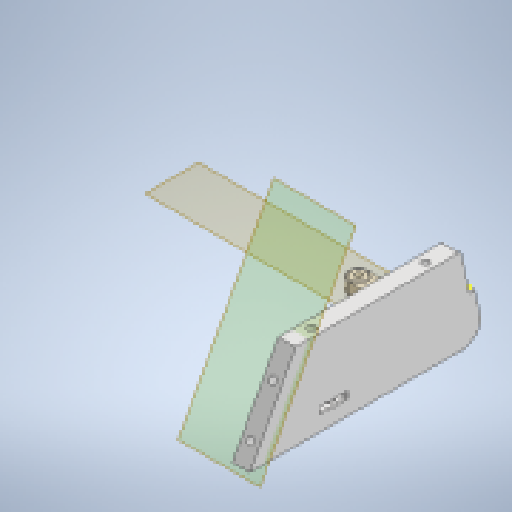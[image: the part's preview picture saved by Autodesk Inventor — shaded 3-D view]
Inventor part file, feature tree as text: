
AUTODESK INVENTOR PART (.ipt)
format: ipt  version: 2023 (Build 270158000, 158)  size: 718,848 bytes
history: native  units: in
note: dims shown in document units (in); Inventor stores cm internally (conversion verified against a paired STEP export)
features: sketch x35, other x12, extrude x6, projected_geometry x4, fillet x1, reference x1
ambient origin geometry x8: Origin, YZ Plane, XZ Plane, XY Plane, X Axis, Y Axis, Z Axis, Center Point
bodies: Body1 (feature_tree)
feature tree (59):
  other  "sciana_awaryjna.ipt"
  extrude  "Wyciągnięcie proste1"  Depth=0.3937in
  extrude  "Wyciągnięcie proste2"  Depth=0.3937in TaperAngle=0.0deg
  extrude  "Wyciągnięcie proste3"  Depth=0.0039in TaperAngle=0.0deg
  extrude  "Wyciągnięcie proste4"  Depth=0.0394in
  fillet  "Zaokrąglenie1"  Radius=0.0197in
  extrude  "Wyciągnięcie proste5"  TaperAngle=0.0deg  [1 undecoded]
  extrude  "Wyciągnięcie proste6"  Depth=0.0118in
  other  "Bryła1::sciana_awaryjna.ipt"
  other  "Bryła wyprowadzona1"
  sketch  "Szkic1"
  sketch  "Szkic2"
  sketch  "Szkic3"
  sketch  "Szkic4"
  sketch  "Szkic5"
  sketch  "Szkic6"
  sketch  "Szkic7"
  sketch  "Szkic8"
  sketch  "Szkic9"
  sketch  "Szkic12"
  sketch  "Szkic13"
  sketch  "Szkic14"
  sketch  "Szkic15"
  sketch  "Szkic16"
  sketch  "Szkic17"
  sketch  "Szkic18"
  sketch  "Szkic19"
  sketch  "Szkic20"
  sketch  "Szkic21"
  sketch  "Szkic22"
  sketch  "Szkic23"
  sketch  "Szkic24"
  sketch  "Szkic25"
  sketch  "Szkic26"
  sketch  "Szkic27"
  sketch  "Szkic28"
  sketch  "Szkic29"
  sketch  "Szkic30"
  sketch  "Szkic31"
  other  "Płaszczyzna konstrukcyjna1"
  other  "Płaszczyzna konstrukcyjna2"
  other  "Płaszczyzna konstrukcyjna3"
  other  "Płaszczyzna konstrukcyjna4"
  sketch  "Szkic32"
  projected_geometry  "Pętla rzutowana1"
  sketch  "Szkic33"
  projected_geometry  "Pętla rzutowana2"
  sketch  "Szkic34"
  reference  "Odniesienie1"
  sketch  "Szkic35"
  sketch  "Szkic36"
  projected_geometry  "Pętla rzutowana3"
  projected_geometry  "Pętla rzutowana4"
  sketch  "Szkic37"
  other  "Bryła1"
  other  "<userpath>\Desktop\MojeRoboty\Stefan\mechanics 2\STEFAN.iam"
  other  "STEFAN.iam"
  other  "plytka_dol:1"
  other  "wlacznik:1"
note: 1 required parameter value undecoded (feature->parameter linkage not recoverable at this tier; creation-order binding heuristic only, values carry confidence <= 0.55)
